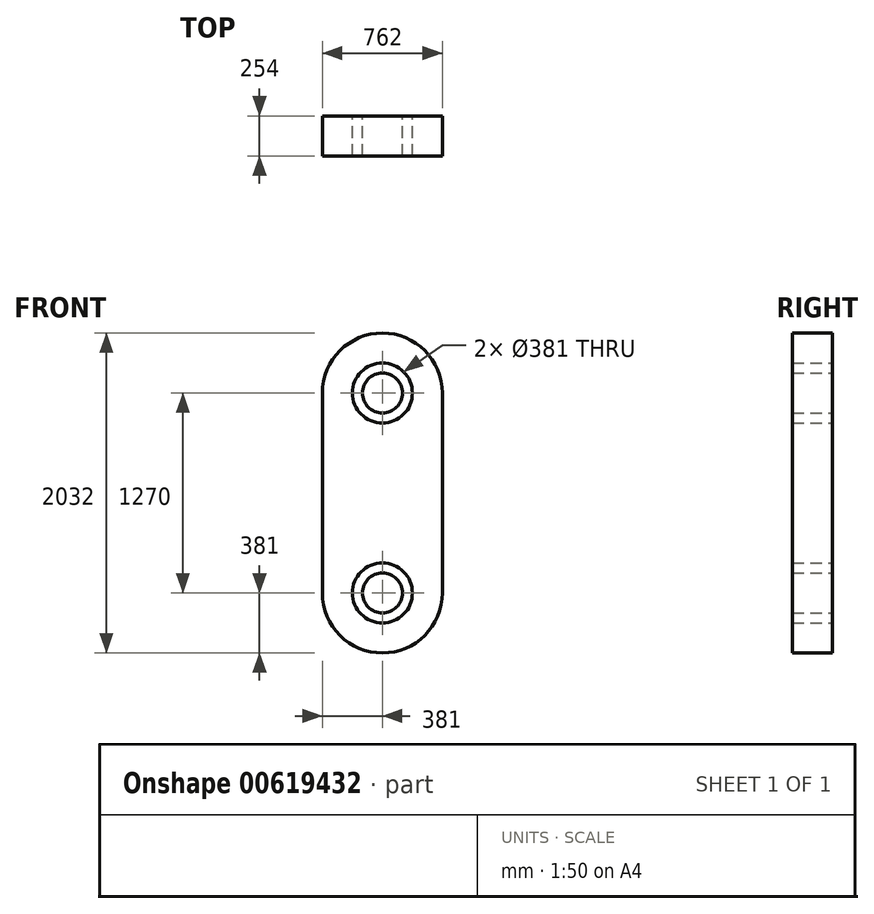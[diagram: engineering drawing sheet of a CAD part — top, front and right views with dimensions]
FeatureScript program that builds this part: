
annotation { "Feature Type Name" : "Feature", "Feature Type Description" : "" }
export const myFeature = defineFeature(function(context is Context, id is Id, definition is map)
    precondition{}
    {
        {
            var Q0;
            Q0=qCreatedBy(makeId("Front.planeOp"),FACE);
            var sketch = newSketch(context, id + "F0", { "sketchPlane" : qUnion([Q0])});
            skLineSegment(sketch, "E0.left", {"start": v(-381, 635) * mm, "end": v(-381, -635) * mm});
            skLineSegment(sketch, "E0.right", {"start": v(381, 635) * mm, "end": v(381, -635) * mm});
            skPoint(sketch, "E0.middle", {"position": v(0, 0) * mm});
            skArc(sketch, "E1", {"start": v(381, 635) * mm, "mid": v(0, 1016) * mm, "end": v(-381, 635) * mm});
            skArc(sketch, "E2", {"start": v(-381, -635) * mm, "mid": v(0, -1016) * mm, "end": v(381, -635) * mm});
            skCircle(sketch, "E3", {"center": v(0, 635) * mm, "radius": 190.5 * mm});
            skCircle(sketch, "E4", {"center": v(0, -635) * mm, "radius": 190.5 * mm});
            skLineSegment(sketch, "E5", {"start": v(0, 1016) * mm, "end": v(0, -1016) * mm, "construction": true});
            skCircle(sketch, "E6", {"center": v(0, 635) * mm, "radius": 127 * mm});
            skCircle(sketch, "E7", {"center": v(0, -635) * mm, "radius": 127 * mm});
            skSolve(sketch);
        }
        {
            var Q0;
            Q0=qSketchRegion(id+"F0",true);
            var Q1;
            Q1=makeQuery(id+"F0.imprint","IMPRINT",FACE,{"disambiguationData":[TD([[makeQuery(id+"F0.imprint","IMPRINT",EDGE,{"derivedFrom":sQuery(id+"F0.wireOp",EDGE,"E7")}),1.0]])]});
            var Q2;
            Q2=makeQuery(id+"F0.imprint","IMPRINT",FACE,{"disambiguationData":[TD([[makeQuery(id+"F0.imprint","IMPRINT",EDGE,{"derivedFrom":sQuery(id+"F0.wireOp",EDGE,"E6")}),1.0]])]});
            extrude(context, id + "F1", {"entities" : qUnion([Q0, Q1, Q2]), "depth" : 254 * mm, "offsetDistance" : 25.4 * mm});
        }
    });
